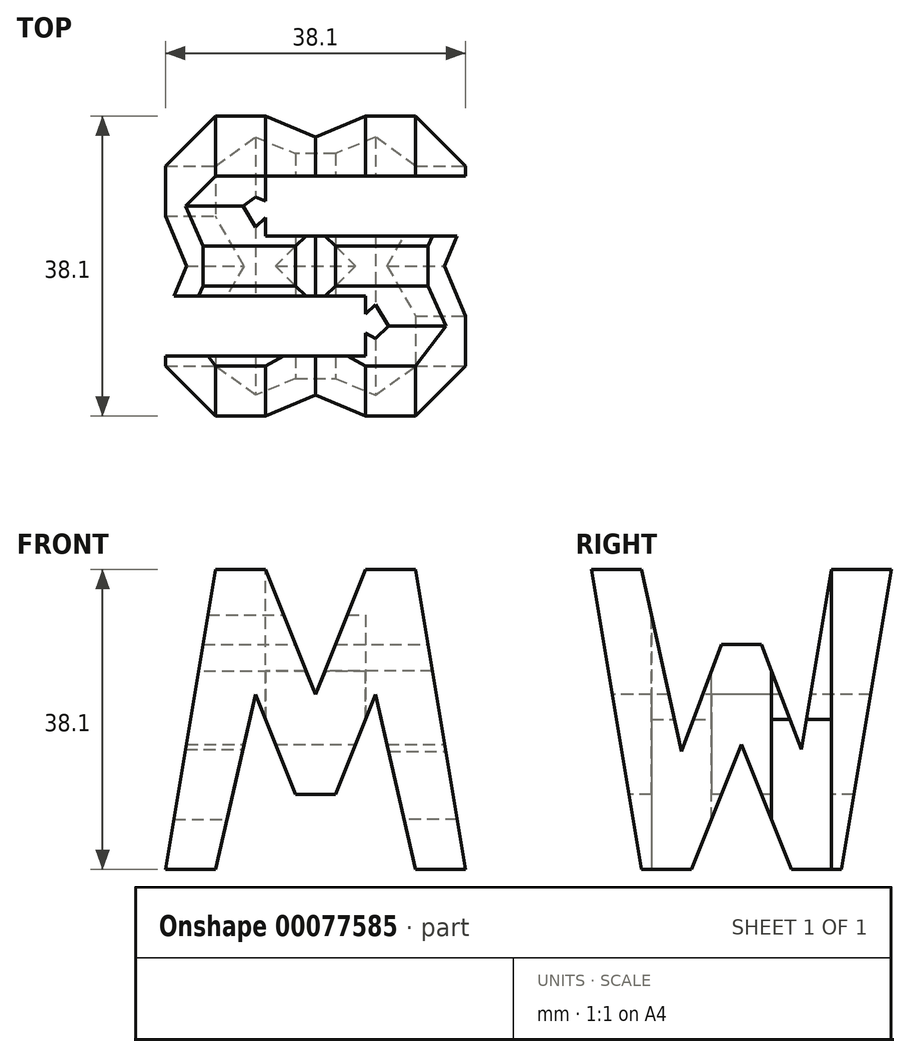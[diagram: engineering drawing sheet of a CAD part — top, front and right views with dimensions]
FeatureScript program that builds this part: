
annotation { "Feature Type Name" : "Feature", "Feature Type Description" : "" }
export const myFeature = defineFeature(function(context is Context, id is Id, definition is map)
    precondition{}
    {
        {
            var Q0;
            Q0=qCreatedBy(makeId("Front.planeOp"),FACE);
            var sketch = newSketch(context, id + "F0", { "sketchPlane" : qUnion([Q0])});
            skLineSegment(sketch, "E0", {"start": v(0, 38.1) * mm, "end": v(0, 0) * mm});
            skLineSegment(sketch, "E1", {"start": v(0, 38.1) * mm, "end": v(38.1, 38.1) * mm});
            skLineSegment(sketch, "E2", {"start": v(38.1, 38.1) * mm, "end": v(38.1, 0) * mm});
            skLineSegment(sketch, "E3", {"start": v(38.1, 0) * mm, "end": v(0, 0) * mm});
            skSolve(sketch);
        }
        {
            var Q0;
            Q0=makeQuery(id+"F0.imprint","IMPRINT",FACE,{"disambiguationData":[TD([[makeQuery(id+"F0.imprint","IMPRINT",EDGE,{"derivedFrom":sQuery(id+"F0.wireOp",EDGE,"E0")}),1.0]])]});
            extrude(context, id + "F1", {"entities" : qUnion([Q0]), "depth" : 38.1 * mm});
        }
        {
            var Q0;
            Q0=qCreatedBy(makeId("Front.planeOp"),FACE);
            cPlane(context, id + "F2", {"entities" : qUnion([Q0]), "cplaneType" : CPlaneType.OFFSET, "offset" : 38.1 * mm, "width" : 152.4 * mm, "height" : 152.4 * mm});
        }
        {
            var Q0;
            Q0=qCreatedBy(makeId("Top.planeOp"),FACE);
            cPlane(context, id + "F3", {"entities" : qUnion([Q0]), "cplaneType" : CPlaneType.OFFSET, "offset" : 38.1 * mm, "width" : 152.4 * mm, "height" : 152.4 * mm});
        }
        {
            var Q0;
            Q0=qCreatedBy(makeId("Right.planeOp"),FACE);
            cPlane(context, id + "F4", {"entities" : qUnion([Q0]), "cplaneType" : CPlaneType.OFFSET, "offset" : 38.1 * mm, "width" : 152.4 * mm, "height" : 152.4 * mm});
        }
        {
            var Q0;
            Q0=qCreatedBy(id+"F4.planeOp",FACE);
            var sketch = newSketch(context, id + "F5", { "sketchPlane" : qUnion([Q0])});
            skLineSegment(sketch, "E4", {"start": v(0, 0) * mm, "end": v(0, 38.1) * mm});
            skLineSegment(sketch, "E5", {"start": v(-38.1, 38.1) * mm, "end": v(0, 38.1) * mm});
            skLineSegment(sketch, "E6", {"start": v(-38.1, 38.1) * mm, "end": v(-38.1, 0) * mm});
            skLineSegment(sketch, "E7", {"start": v(0, 0) * mm, "end": v(-38.1, 0) * mm});
            skLineSegment(sketch, "E8", {"start": v(-19.05, 15.87) * mm, "end": v(-12.7, 0) * mm});
            skLineSegment(sketch, "E9", {"start": v(-6.35, 0) * mm, "end": v(0, 38.1) * mm});
            skLineSegment(sketch, "E10", {"start": v(-38.1, 38.1) * mm, "end": v(-31.75, 0) * mm});
            skLineSegment(sketch, "E11", {"start": v(-19.05, 15.87) * mm, "end": v(-25.4, 0) * mm});
            skLineSegment(sketch, "E12", {"start": v(-31.75, 38.1) * mm, "end": v(-26.67, 14.97) * mm});
            skLineSegment(sketch, "E13", {"start": v(-26.67, 14.97) * mm, "end": v(-21.59, 28.57) * mm});
            skLineSegment(sketch, "E14", {"start": v(-21.59, 28.57) * mm, "end": v(-16.5, 28.57) * mm});
            skLineSegment(sketch, "E15", {"start": v(-16.5, 28.57) * mm, "end": v(-11.43, 15.25) * mm});
            skLineSegment(sketch, "E16", {"start": v(-11.43, 15.25) * mm, "end": v(-7.63, 38.1) * mm});
            skSolve(sketch);
        }
        {
            var Q0;
            {var subQ1=sQuery(id+"F5.wireOp",EDGE,"E12");Q0=makeQuery(id+"F5.imprint","IMPRINT",FACE,{"disambiguationData":[TD([[makeQuery(id+"F5.imprint","IMPRINT",EDGE,{"derivedFrom":subQ1}),1.0]])]});}
            var Q1;
            {var subQ0=sQuery(id+"F5.wireOp",EDGE,"E6");Q1=makeQuery(id+"F5.imprint","IMPRINT",FACE,{"disambiguationData":[TD([[makeQuery(id+"F5.imprint","IMPRINT",EDGE,{"derivedFrom":subQ0}),1.0]])]});}
            var Q2;
            {var subQ0=sQuery(id+"F5.wireOp",EDGE,"E8");Q2=makeQuery(id+"F5.imprint","IMPRINT",FACE,{"disambiguationData":[TD([[makeQuery(id+"F5.imprint","IMPRINT",EDGE,{"derivedFrom":subQ0}),-1.0]])]});}
            var Q3;
            {var subQ0=sQuery(id+"F5.wireOp",EDGE,"E4");Q3=makeQuery(id+"F5.imprint","IMPRINT",FACE,{"disambiguationData":[TD([[makeQuery(id+"F5.imprint","IMPRINT",EDGE,{"derivedFrom":subQ0}),1.0]])]});}
            extrude(context, id + "F6", {"entities" : qUnion([Q0, Q1, Q2, Q3]), "operationType" : NewBodyOperationType.REMOVE, "oppositeDirection" : true, "depth" : 38.1 * mm});
        }
        {
            var Q0;
            Q0=qCreatedBy(id+"F2.planeOp",FACE);
            var sketch = newSketch(context, id + "F7", { "sketchPlane" : qUnion([Q0])});
            skLineSegment(sketch, "E17", {"start": v(0, 38.1) * mm, "end": v(38.1, 38.1) * mm});
            skLineSegment(sketch, "E18", {"start": v(38.1, 38.1) * mm, "end": v(38.1, 0) * mm});
            skLineSegment(sketch, "E19", {"start": v(38.1, 0) * mm, "end": v(0, 0) * mm});
            skLineSegment(sketch, "E20", {"start": v(6.35, 38.1) * mm, "end": v(0, 0) * mm});
            skLineSegment(sketch, "E21", {"start": v(16.51, 9.52) * mm, "end": v(21.6, 9.52) * mm});
            skLineSegment(sketch, "E22", {"start": v(21.6, 9.52) * mm, "end": v(26.67, 22.22) * mm});
            skLineSegment(sketch, "E23", {"start": v(26.67, 22.22) * mm, "end": v(31.75, 0) * mm});
            skLineSegment(sketch, "E24", {"start": v(38.1, 0) * mm, "end": v(31.75, 38.1) * mm});
            skLineSegment(sketch, "E25", {"start": v(25.4, 38.1) * mm, "end": v(19.05, 22.22) * mm});
            skLineSegment(sketch, "E26", {"start": v(12.7, 38.1) * mm, "end": v(19.05, 22.22) * mm});
            skLineSegment(sketch, "E27", {"start": v(0, 38.1) * mm, "end": v(0, 0) * mm});
            skLineSegment(sketch, "E28", {"start": v(16.51, 9.52) * mm, "end": v(11.43, 22.22) * mm});
            skLineSegment(sketch, "E29", {"start": v(11.43, 22.22) * mm, "end": v(6.35, 0) * mm});
            skSolve(sketch);
        }
        {
            var Q0;
            {var subQ2=sQuery(id+"F7.wireOp",EDGE,"E20");Q0=makeQuery(id+"F7.imprint","IMPRINT",FACE,{"disambiguationData":[TD([[makeQuery(id+"F7.imprint","IMPRINT",EDGE,{"derivedFrom":subQ2}),-1.0]])]});}
            var Q1;
            {var subQ0=sQuery(id+"F7.wireOp",EDGE,"E25");Q1=makeQuery(id+"F7.imprint","IMPRINT",FACE,{"disambiguationData":[TD([[makeQuery(id+"F7.imprint","IMPRINT",EDGE,{"derivedFrom":subQ0}),-1.0]])]});}
            var Q2;
            {var subQ0=sQuery(id+"F7.wireOp",EDGE,"E18");Q2=makeQuery(id+"F7.imprint","IMPRINT",FACE,{"disambiguationData":[TD([[makeQuery(id+"F7.imprint","IMPRINT",EDGE,{"derivedFrom":subQ0}),-1.0]])]});}
            var Q3;
            Q3=makeQuery(id+"F7.imprint","IMPRINT",FACE,{"disambiguationData":[TD([[makeQuery(id+"F7.imprint","IMPRINT",EDGE,{"derivedFrom":sQuery(id+"F7.wireOp",EDGE,"E21")}),-1.0]])]});
            extrude(context, id + "F8", {"entities" : qUnion([Q0, Q1, Q2, Q3]), "operationType" : NewBodyOperationType.REMOVE, "oppositeDirection" : true, "depth" : 38.1 * mm});
        }
        {
            var Q0;
            Q0=qCreatedBy(id+"F3.planeOp",FACE);
            var sketch = newSketch(context, id + "F9", { "sketchPlane" : qUnion([Q0])});
            skLineSegment(sketch, "E30", {"start": v(0, 0) * mm, "end": v(0, -38.1) * mm});
            skLineSegment(sketch, "E31", {"start": v(0, -38.1) * mm, "end": v(38.1, -38.1) * mm});
            skLineSegment(sketch, "E32", {"start": v(38.1, -38.1) * mm, "end": v(38.1, 0) * mm});
            skLineSegment(sketch, "E33", {"start": v(38.1, 0) * mm, "end": v(0, 0) * mm});
            skLineSegment(sketch, "E34", {"start": v(12.7, -7.62) * mm, "end": v(38.1, -7.62) * mm});
            skLineSegment(sketch, "E35", {"start": v(12.7, -7.62) * mm, "end": v(12.7, -15.24) * mm});
            skLineSegment(sketch, "E36", {"start": v(12.7, -15.24) * mm, "end": v(38.1, -15.24) * mm});
            skLineSegment(sketch, "E37", {"start": v(0, -22.86) * mm, "end": v(25.4, -22.86) * mm});
            skLineSegment(sketch, "E38", {"start": v(25.4, -22.86) * mm, "end": v(25.4, -30.48) * mm});
            skLineSegment(sketch, "E39", {"start": v(25.4, -30.48) * mm, "end": v(0, -30.48) * mm});
            skSolve(sketch);
        }
        {
            var Q0;
            {var subQ0=sQuery(id+"F9.wireOp",EDGE,"E34");Q0=makeQuery(id+"F9.imprint","IMPRINT",FACE,{"disambiguationData":[TD([[makeQuery(id+"F9.imprint","IMPRINT",EDGE,{"derivedFrom":subQ0}),-1.0]])]});}
            var Q1;
            {var subQ0=sQuery(id+"F9.wireOp",EDGE,"E37");Q1=makeQuery(id+"F9.imprint","IMPRINT",FACE,{"disambiguationData":[TD([[makeQuery(id+"F9.imprint","IMPRINT",EDGE,{"derivedFrom":subQ0}),-1.0]])]});}
            extrude(context, id + "F10", {"entities" : qUnion([Q0, Q1]), "operationType" : NewBodyOperationType.REMOVE, "oppositeDirection" : true, "depth" : 38.1 * mm});
        }
    });
